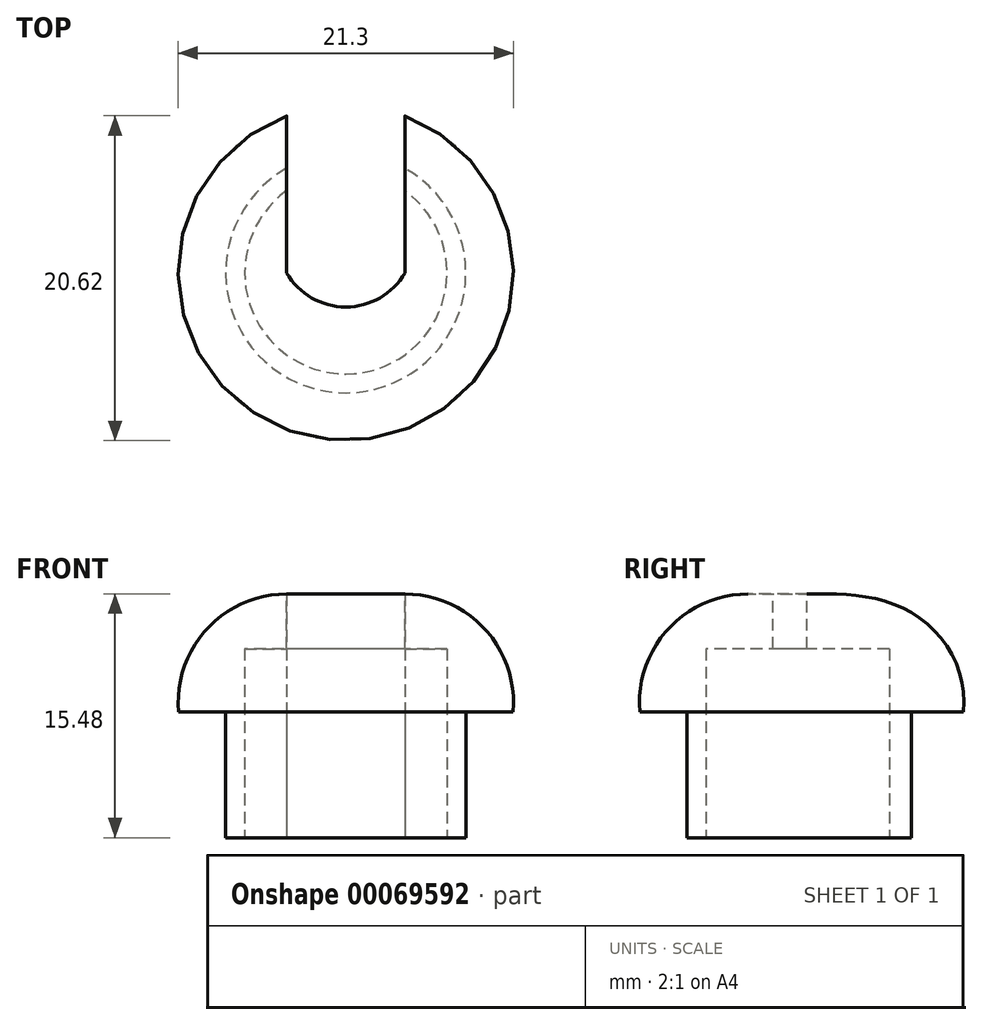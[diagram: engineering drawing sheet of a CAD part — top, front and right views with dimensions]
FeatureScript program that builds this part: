
annotation { "Feature Type Name" : "Feature", "Feature Type Description" : "" }
export const myFeature = defineFeature(function(context is Context, id is Id, definition is map)
    precondition{}
    {
        {
            var Q0;
            Q0=qCreatedBy(makeId("Top.planeOp"),FACE);
            var sketch = newSketch(context, id + "F0", { "sketchPlane" : qUnion([Q0])});
            skCircle(sketch, "E0", {"center": v(0, 0) * mm, "radius": 7.63 * mm});
            skSolve(sketch);
        }
        {
            var Q0;
            Q0=qCreatedBy(makeId("Front.planeOp"),FACE);
            var sketch = newSketch(context, id + "F1", { "sketchPlane" : qUnion([Q0])});
            skLineSegment(sketch, "E1.0", {"start": v(-7.63, 0) * mm, "end": v(7.63, 0) * mm});
            skLineSegment(sketch, "E2", {"start": v(7.63, 0) * mm, "end": v(7.63, 8) * mm});
            skLineSegment(sketch, "E3", {"start": v(0, 0) * mm, "end": v(0, 15.48) * mm});
            skLineSegment(sketch, "E4", {"start": v(7.63, 8) * mm, "end": v(10.63, 8) * mm});
            skLineSegment(sketch, "E5", {"start": v(0, 15.48) * mm, "end": v(3.75, 15.48) * mm});
            skArc(sketch, "E6", {"start": v(10.63, 8) * mm, "mid": v(8.83, 13.25) * mm, "end": v(3.75, 15.48) * mm});
            skSolve(sketch);
        }
        {
            var Q0;
            {var subQ0=sQuery(id+"F1.wireOp",EDGE,"E2");Q0=makeQuery(id+"F1.imprint","IMPRINT",FACE,{"disambiguationData":[TD([[makeQuery(id+"F1.imprint","IMPRINT",EDGE,{"derivedFrom":subQ0}),1.0]])]});}
            var Q1;
            Q1=sQuery(id+"F0.wireOp",EDGE,"E0");
            revolve(context, id + "F2", {"entities" : qUnion([Q0]), "axis" : qUnion([Q1]), "revolveType" : RevolveType.FULL});
        }
        {
            var Q0;
            Q0=makeQuery(id+"F2.opRevolve","SWEPT_FACE",FACE,{"disambiguationData":[OSD([sQuery(id+"F1.wireOp",EDGE,"E5")])]});
            var sketch = newSketch(context, id + "F3", { "sketchPlane" : qUnion([Q0])});
            skCircle(sketch, "E7.0", {"center": v(0, 0) * mm, "radius": 10.63 * mm});
            skLineSegment(sketch, "E8", {"start": v(-3.75, 0) * mm, "end": v(-3.75, 9.94) * mm});
            skLineSegment(sketch, "E9", {"start": v(3.75, 0) * mm, "end": v(3.75, 9.94) * mm});
            skArc(sketch, "E10", {"start": v(-3.75, 0) * mm, "mid": v(0, -2.17) * mm, "end": v(3.75, 0) * mm});
            skLineSegment(sketch, "E11", {"start": v(-3.75, 9.94) * mm, "end": v(-3.75, 12.18) * mm});
            skLineSegment(sketch, "E12", {"start": v(-3.75, 12.18) * mm, "end": v(3.75, 12.18) * mm});
            skLineSegment(sketch, "E13", {"start": v(3.75, 12.18) * mm, "end": v(3.75, 9.94) * mm});
            skSolve(sketch);
        }
        {
            var Q0;
            {var subQ0=sQuery(id+"F3.wireOp",EDGE,"E10");Q0=makeQuery(id+"F3.imprint","IMPRINT",FACE,{"disambiguationData":[TD([[makeQuery(id+"F3.imprint","IMPRINT",EDGE,{"derivedFrom":subQ0}),1.0]])]});}
            var Q1;
            {var subQ0=sQuery(id+"F3.wireOp",EDGE,"E8");Q1=makeQuery(id+"F3.imprint","IMPRINT",FACE,{"disambiguationData":[TD([[makeQuery(id+"F3.imprint","IMPRINT",EDGE,{"derivedFrom":subQ0}),-1.0]])]});}
            var Q2;
            {var subQ0=sQuery(id+"F3.wireOp",EDGE,"E11");Q2=makeQuery(id+"F3.imprint","IMPRINT",FACE,{"disambiguationData":[TD([[makeQuery(id+"F3.imprint","IMPRINT",EDGE,{"derivedFrom":subQ0}),-1.0]])]});}
            extrude(context, id + "F4", {"entities" : qUnion([Q0, Q1, Q2]), "operationType" : NewBodyOperationType.REMOVE, "endBound" : BoundingType.THROUGH_ALL, "oppositeDirection" : true, "depth" : 25 * mm});
        }
        {
            var Q0;
            Q0=makeQuery(id+"F2.opRevolve","SWEPT_FACE",FACE,{"disambiguationData":[OSD([sQuery(id+"F1.wireOp",EDGE,"E1.0")])]});
            var sketch = newSketch(context, id + "F5", { "sketchPlane" : qUnion([Q0])});
            skCircle(sketch, "E14", {"center": v(0, 0) * mm, "radius": 6.43 * mm});
            skArc(sketch, "E15.0", {"start": v(3.75, -6.64) * mm, "mid": v(0, 7.63) * mm, "end": v(-3.75, -6.64) * mm});
            skSolve(sketch);
        }
        {
            var Q0;
            {var subQ1=makeQuery(id+"F2.opRevolve","SWEPT_FACE",FACE,{"disambiguationData":[OSD([sQuery(id+"F1.wireOp",EDGE,"E1.0")])]});var subQ6=makeQuery(id+"F4.boolean.opBoolean","INTERSECT",EDGE,{"derivedFrom":[subQ1,makeQuery(id+"F4.opExtrude","SWEPT_FACE",FACE,{"disambiguationData":[OSD([sQuery(id+"F3.wireOp",EDGE,"E10")])]})]});Q0=makeQuery(id+"F5.imprint","IMPRINT",FACE,{"disambiguationData":[TD([[makeQuery(id+"F5.imprint","IMPRINT",EDGE,{"derivedFrom":subQ6}),-1.0]])]});}
            extrude(context, id + "F6", {"entities" : qUnion([Q0]), "operationType" : NewBodyOperationType.REMOVE, "oppositeDirection" : true, "depth" : 12 * mm});
        }
    });
